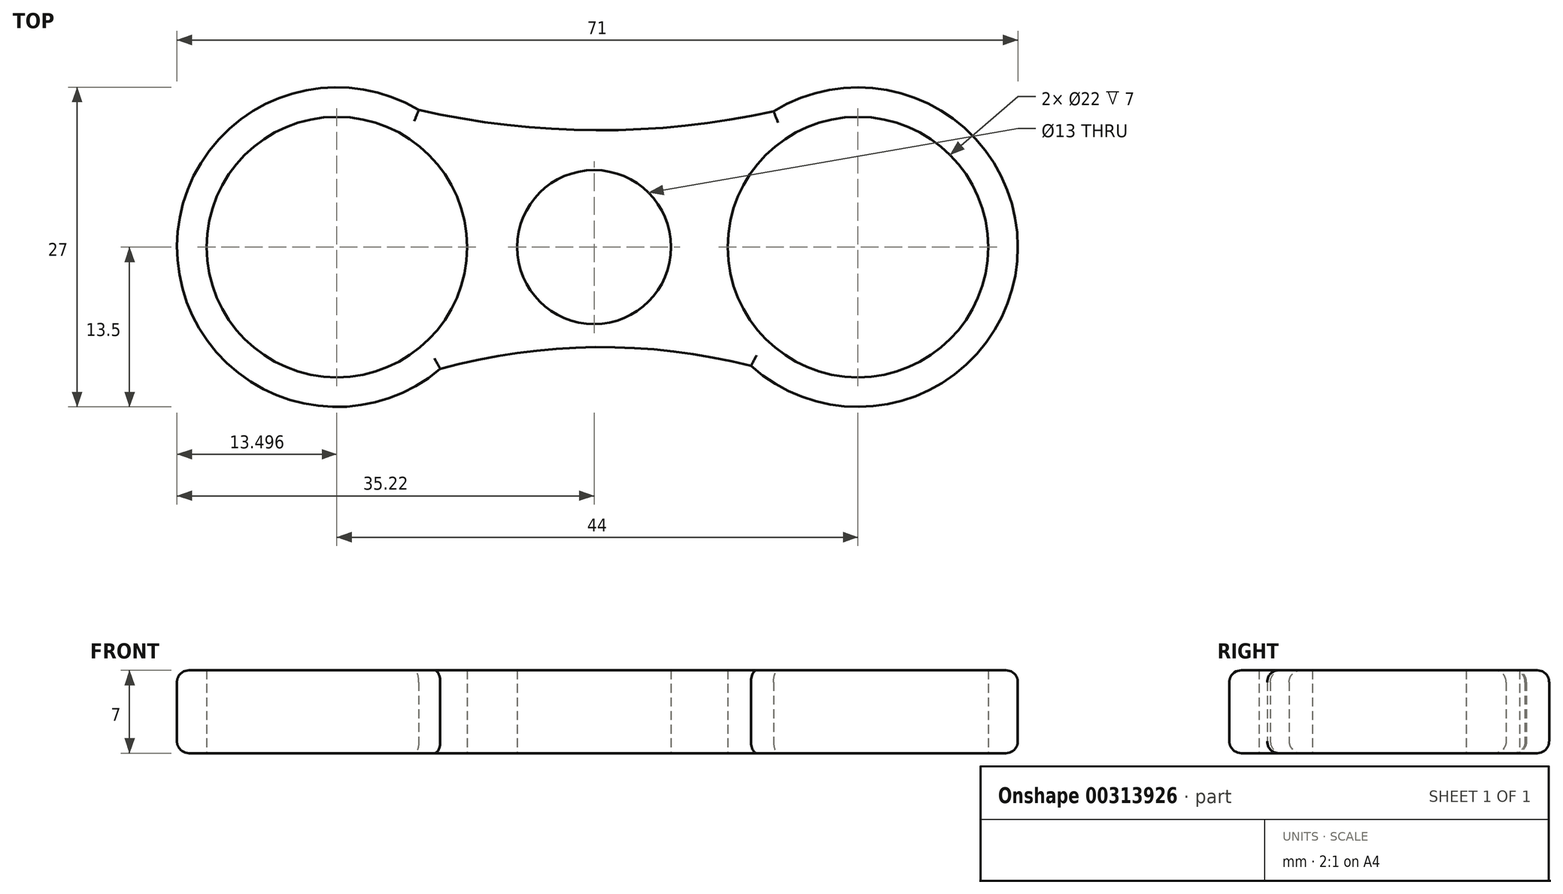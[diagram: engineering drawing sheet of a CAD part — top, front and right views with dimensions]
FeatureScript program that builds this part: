
annotation { "Feature Type Name" : "Feature", "Feature Type Description" : "" }
export const myFeature = defineFeature(function(context is Context, id is Id, definition is map)
    precondition{}
    {
        {
            var Q0;
            Q0=qCreatedBy(makeId("Top.planeOp"),FACE);
            var sketch = newSketch(context, id + "F0", { "sketchPlane" : qUnion([Q0])});
            skCircle(sketch, "E0", {"center": v(-21.72, 0) * mm, "radius": 11 * mm});
            skCircle(sketch, "E1", {"center": v(22.28, 0) * mm, "radius": 11 * mm});
            skCircle(sketch, "E2", {"center": v(-21.72, 0) * mm, "radius": 13.5 * mm});
            skCircle(sketch, "E3", {"center": v(22.28, 0) * mm, "radius": 13.5 * mm});
            skPoint(sketch, "E4.middle", {"position": v(0, 0) * mm});
            skCircle(sketch, "E5", {"center": v(0, 0) * mm, "radius": 6.5 * mm});
            skArc(sketch, "E6", {"start": v(-21.54, 13.5) * mm, "mid": v(0.45, 9.87) * mm, "end": v(22.44, 13.5) * mm});
            skArc(sketch, "E7", {"start": v(22.77, -13.5) * mm, "mid": v(0.61, -8.45) * mm, "end": v(-21.54, -13.5) * mm});
            skSolve(sketch);
        }
        {
            var Q0;
            {var subQ0=sQuery(id+"F0.wireOp",EDGE,"E6");var subQ1=sQuery(id+"F0.wireOp",EDGE,"E2");var subQ2=makeQuery(id+"F0.imprint","INTERSECT",VERTEX,{"disambiguationData":[OD(0.0)],"derivedFrom":[subQ1,subQ0]});Q0=makeQuery(id+"F0.imprint","IMPRINT",FACE,{"disambiguationData":[TD([[makeQuery(id+"F0.imprint","IMPRINT",EDGE,{"disambiguationData":[TD([[subQ2,1.0]])],"derivedFrom":subQ1}),1.0]])]});}
            var Q1;
            {var subQ0=sQuery(id+"F0.wireOp",EDGE,"E7");var subQ1=sQuery(id+"F0.wireOp",EDGE,"E2");var subQ2=makeQuery(id+"F0.imprint","INTERSECT",VERTEX,{"disambiguationData":[OD(0.0)],"derivedFrom":[subQ1,subQ0]});Q1=makeQuery(id+"F0.imprint","IMPRINT",FACE,{"disambiguationData":[TD([[makeQuery(id+"F0.imprint","IMPRINT",EDGE,{"disambiguationData":[TD([[subQ2,-1.0]])],"derivedFrom":subQ1}),1.0]])]});}
            var Q2;
            {var subQ0=sQuery(id+"F0.wireOp",EDGE,"E6");var subQ1=sQuery(id+"F0.wireOp",EDGE,"E3");var subQ2=makeQuery(id+"F0.imprint","INTERSECT",VERTEX,{"disambiguationData":[OD(0.0)],"derivedFrom":[subQ1,subQ0]});Q2=makeQuery(id+"F0.imprint","IMPRINT",FACE,{"disambiguationData":[TD([[makeQuery(id+"F0.imprint","IMPRINT",EDGE,{"disambiguationData":[TD([[subQ2,-1.0]])],"derivedFrom":subQ1}),1.0]])]});}
            var Q3;
            {var subQ0=sQuery(id+"F0.wireOp",EDGE,"E7");var subQ1=sQuery(id+"F0.wireOp",EDGE,"E3");var subQ2=makeQuery(id+"F0.imprint","INTERSECT",VERTEX,{"disambiguationData":[OD(0.0)],"derivedFrom":[subQ1,subQ0]});Q3=makeQuery(id+"F0.imprint","IMPRINT",FACE,{"disambiguationData":[TD([[makeQuery(id+"F0.imprint","IMPRINT",EDGE,{"disambiguationData":[TD([[subQ2,1.0]])],"derivedFrom":subQ1}),1.0]])]});}
            var Q4;
            Q4=makeQuery(id+"F0.imprint","IMPRINT",FACE,{"disambiguationData":[TD([[makeQuery(id+"F0.imprint","IMPRINT",EDGE,{"derivedFrom":sQuery(id+"F0.wireOp",EDGE,"E0")}),-1.0]])]});
            var Q5;
            Q5=makeQuery(id+"F0.imprint","IMPRINT",FACE,{"disambiguationData":[TD([[makeQuery(id+"F0.imprint","IMPRINT",EDGE,{"derivedFrom":sQuery(id+"F0.wireOp",EDGE,"E1")}),-1.0]])]});
            var Q6;
            Q6=makeQuery(id+"F0.imprint","IMPRINT",FACE,{"disambiguationData":[TD([[makeQuery(id+"F0.imprint","IMPRINT",EDGE,{"derivedFrom":sQuery(id+"F0.wireOp",EDGE,"E5")}),-1.0]])]});
            extrude(context, id + "F1", {"entities" : qUnion([Q0, Q1, Q2, Q3, Q4, Q5, Q6]), "endBound" : BoundingType.SYMMETRIC, "depth" : 7 * mm});
        }
        {
            var Q0;
            Q0=makeQuery(id+"F1.opExtrude","CAP_EDGE",EDGE,{"disambiguationData":[OSD([sQuery(id+"F0.wireOp",EDGE,"E3")])],"isStart":true});
            var Q1;
            Q1=makeQuery(id+"F1.opExtrude","CAP_EDGE",EDGE,{"disambiguationData":[OSD([sQuery(id+"F0.wireOp",EDGE,"E6")])],"isStart":true});
            var Q2;
            Q2=makeQuery(id+"F1.opExtrude","CAP_EDGE",EDGE,{"disambiguationData":[OSD([sQuery(id+"F0.wireOp",EDGE,"E2")])],"isStart":true});
            var Q3;
            Q3=makeQuery(id+"F1.opExtrude","CAP_EDGE",EDGE,{"disambiguationData":[OSD([sQuery(id+"F0.wireOp",EDGE,"E7")])],"isStart":true});
            var Q4;
            Q4=makeQuery(id+"F1.opExtrude","CAP_EDGE",EDGE,{"disambiguationData":[OSD([sQuery(id+"F0.wireOp",EDGE,"E3")])],"isStart":false});
            var Q5;
            Q5=makeQuery(id+"F1.opExtrude","CAP_EDGE",EDGE,{"disambiguationData":[OSD([sQuery(id+"F0.wireOp",EDGE,"E7")])],"isStart":false});
            var Q6;
            Q6=makeQuery(id+"F1.opExtrude","CAP_EDGE",EDGE,{"disambiguationData":[OSD([sQuery(id+"F0.wireOp",EDGE,"E6")])],"isStart":false});
            var Q7;
            Q7=makeQuery(id+"F1.opExtrude","CAP_EDGE",EDGE,{"disambiguationData":[OSD([sQuery(id+"F0.wireOp",EDGE,"E2")])],"isStart":false});
            fillet(context, id + "F2", {"entities" : qUnion([Q0, Q1, Q2, Q3, Q4, Q5, Q6, Q7]), "radius" : 1 * mm, "tangentPropagation" : true, "allowEdgeOverflow" : false});
        }
    });
